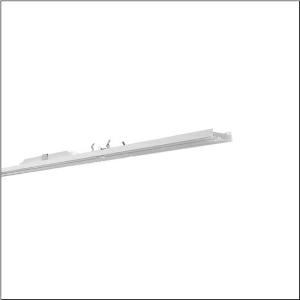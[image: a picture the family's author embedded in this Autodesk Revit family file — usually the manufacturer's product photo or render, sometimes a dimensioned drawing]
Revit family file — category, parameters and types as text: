
# Revit family: licross_r__11_recessed_mo_51ul1edv4e5f_fa7a
name_source: partatom
category: Lighting Fixtures
units: mm (PartAtom-declared; Revit-internal decimal feet)

## family parameters
Cut with Voids When Loaded = No
Host = Face
Light Source = No
Part Type = Normal
Room Calculation Point = No
Round Connector Dimension = Use Diameter
Shared = No

## types (1)
- --- (1 x LED, 14910 lm, 89.6 W, 4000K)
    Apparent Load = 90 VA
    CIE Flux Codes = 85 95 99 100 100
    Color Rendering = 80
    Color Temperature = 4000K
    Default Elevation = 1800 mm
    Description = Licross® 11 Recessed MO, luminaire insert, of sheet steel, galvanised, coil coated, white, length: 2.250mm, width: 66mm, height: 67mm, LED rated luminous flux: 14.910lm, light colour: 840, control gear: DALI 2, control gear: ECG DALI, with terminal, 5-pole, max. 2.5mm², mains connection: 230V, AC, 50/60Hz, rated input power: 90W, halogen-free wiring, primary optical cover: cover, of PMMA, light emission: direct distribution, primary light characteristic: symmetric, protection rating (complete): IP40, insulation class (complete): insulation class I (protective earthing), certification: CE, ENEC, VDE, UKCA, protection symbol: D if used in an environment without relevant dust loads with corresponding accessories, impact resistance: IK06, permissible ambient temperature for indoor applications: -25..+35°C, corresponds to IFS (International Featured Standards) requirements for safety and quality in the food industry, reducing of maximum allowable ambient temperature of 5°C with ceiling mounting, LABS conformity tested according to VDMA 24364:2018-05, packaging unit: 1 piece
    Height = 58 mm
    Lamp = 1 x LED
    Lamp Light Flux = 14910 lm
    Lamp Power = 89.6 W
    Lamp count = 1
    Length = 2250 mm
    Luminous efficacy = 166 lm/W
    Manufacturer = Siteco
    ModVariant = No
    Model = 51UL1EDV4E5F
    Mounting Place = Ceiling
    Mounting Type = Pendant
    Number of Poles = 1
    OnlyDefault = Yes
    Power Factor = 1
    Product Name = Licross® 11 Recessed MO
    Product group = luminaire insert
    ProductGroupID = 901
    Protection Class = Protection class I
    Protection Degree = IP 40
    RLX_Detail_Level = 1
    RLX_Emergency_Light_Flux = 0 lm
    RLX_Emergency_Type = 0
    RLX_Emergency_Type_DB = No
    RlxData = <blob elided: 26741 chars, md5=05f54012>
    Socket = socket
    Standby Power = 0 W
    System Light Flux = 14910 lm
    System Power = 90 W
    Type Comments = factory setting: luminous flux: 100 % | dim-lin: 254 | 400 mA
    Type Image = l_1006953.jpg
    URL = http://relux.com
    VarID = @adj_112439
    Voltage = 0 V
    Weight = 0.00 kg
    Width = 66 mm

## geometry (parser evidence)
native form markers: Blend x4, Sweep x10
no freeform markers — native parametric forms only
